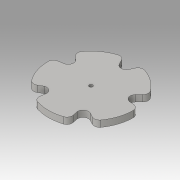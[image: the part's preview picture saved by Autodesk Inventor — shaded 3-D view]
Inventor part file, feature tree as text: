
AUTODESK INVENTOR PART (.ipt)
format: ipt  version: 2016 (Build 200138000, 138)  size: 131,072 bytes
history: native  units: in
note: dims shown in document units (in); Inventor stores cm internally (conversion verified against a paired STEP export)
features: sketch x3, extrude x2, fillet x2, pattern_circular x1, hole x1
ambient origin geometry x8: Origin, YZ Plane, XZ Plane, XY Plane, X Axis, Y Axis, Z Axis, Center Point
bodies: Solid1 (feature_tree)
feature tree (9):
  extrude  "Extrusion1"  Depth=0.45in TaperAngle=0.0deg
  extrude  "Extrusion2"  Depth=0.375in
  fillet  "Fillet1"  [1 undecoded]
  fillet  "Fillet2"  Radius=0.375in
  pattern_circular  "Circular Pattern1"  Count=5 Angle=360.0deg
  hole  "Hole1"  [1 undecoded]
  sketch  "Sketch1"  dims[d0=6.0in d1=0.45in d2=0.0in]
  sketch  "Sketch2"  dims[d3=0.5in d4=0.75in d5=0.0in d6=0.0in d7=0.375in]
  sketch  "Sketch4"  dims[d8=0.375in d9=1.9685in d10=360.0deg d16=1.25in d19=0.25in d20=0.25in d21=0.75in d22=0.375in d23=0.25in d24=0.5635in d25=1.0in d26=0.8108in]
note: 2 required parameter values undecoded (feature->parameter linkage not recoverable at this tier; creation-order binding heuristic only, values carry confidence <= 0.55)
